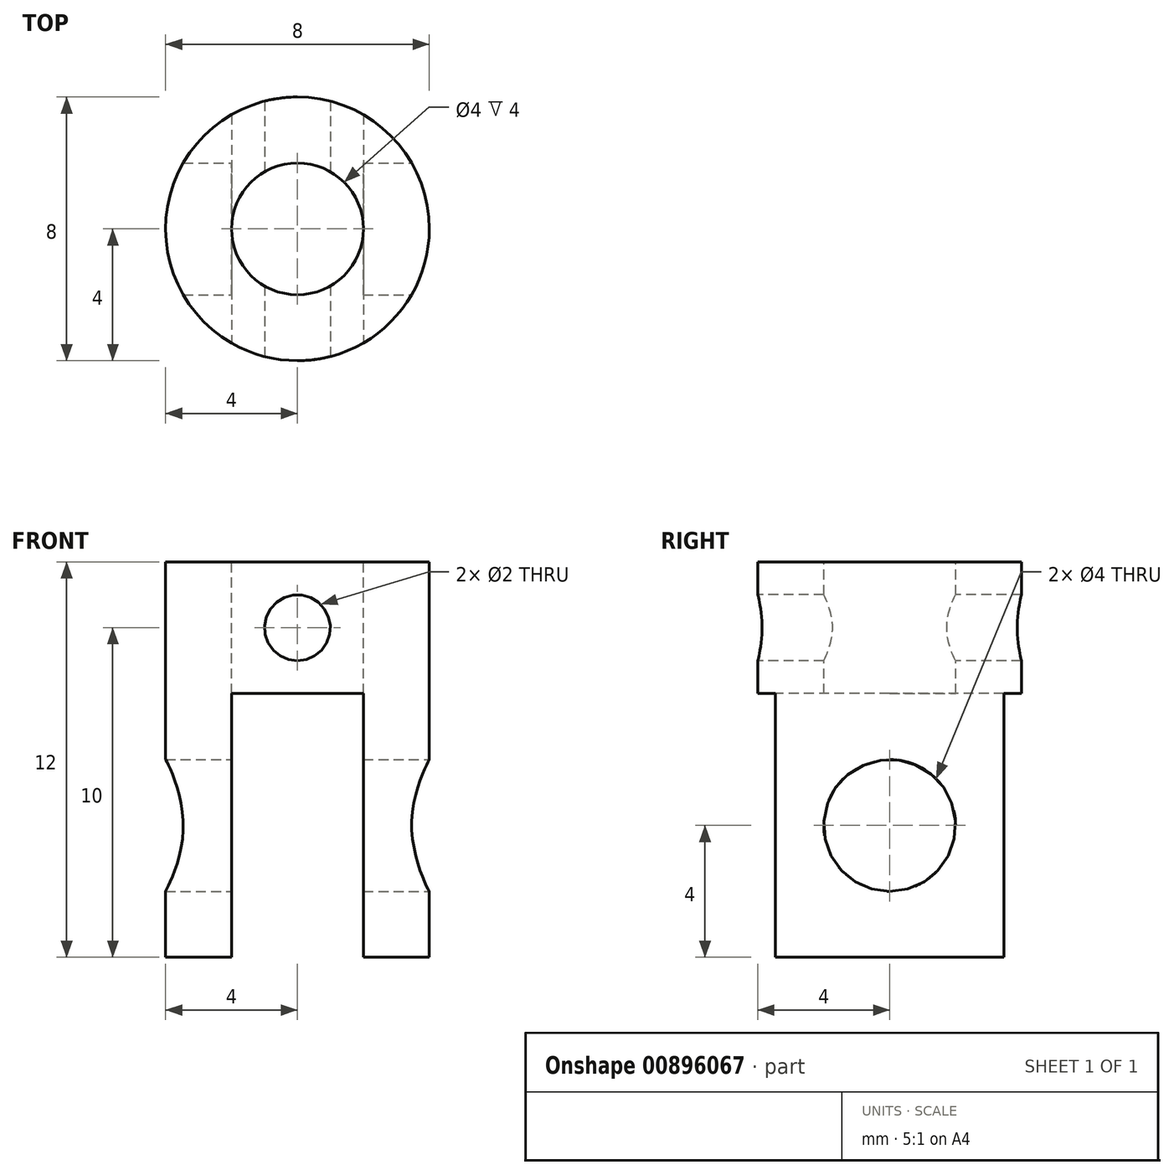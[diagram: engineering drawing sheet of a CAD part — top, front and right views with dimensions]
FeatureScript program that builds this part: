
annotation { "Feature Type Name" : "Feature", "Feature Type Description" : "" }
export const myFeature = defineFeature(function(context is Context, id is Id, definition is map)
    precondition{}
    {
        {
            var Q0;
            Q0=qCreatedBy(makeId("Top.planeOp"),FACE);
            var sketch = newSketch(context, id + "F0", { "sketchPlane" : qUnion([Q0])});
            skCircle(sketch, "E0", {"center": v(0, 0) * mm, "radius": 4 * mm});
            skSolve(sketch);
        }
        {
            var Q0;
            Q0 = qSketchRegion(id + "F0", true);
            extrude(context, id + "F1", {"entities" : qUnion([Q0]), "depth" : 12 * mm, "offsetDistance" : 25 * mm});
        }
        {
            var Q0;
            Q0=qCreatedBy(makeId("Front.planeOp"),FACE);
            var sketch = newSketch(context, id + "F2", { "sketchPlane" : qUnion([Q0])});
            skLineSegment(sketch, "E1.bottom", {"start": v(-2, 0) * mm, "end": v(2, 0) * mm});
            skLineSegment(sketch, "E1.top", {"start": v(-2, 8) * mm, "end": v(2, 8) * mm});
            skLineSegment(sketch, "E1.left", {"start": v(-2, 0) * mm, "end": v(-2, 8) * mm});
            skLineSegment(sketch, "E1.right", {"start": v(2, 0) * mm, "end": v(2, 8) * mm});
            skSolve(sketch);
        }
        {
            var Q0;
            Q0=makeQuery(id+"F2.imprint","IMPRINT",FACE,{"disambiguationData":[TD([[makeQuery(id+"F2.imprint","IMPRINT",EDGE,{"derivedFrom":sQuery(id+"F2.wireOp",EDGE,"E1.bottom")}),1.0]])]});
            extrude(context, id + "F3", {"entities" : qUnion([Q0]), "operationType" : NewBodyOperationType.REMOVE, "endBound" : BoundingType.SYMMETRIC, "oppositeDirection" : true, "depth" : 25 * mm, "offsetDistance" : 25 * mm});
        }
        {
            var Q0;
            Q0=qCreatedBy(makeId("Front.planeOp"),FACE);
            var sketch = newSketch(context, id + "F4", { "sketchPlane" : qUnion([Q0])});
            skCircle(sketch, "E2", {"center": v(0, 10) * mm, "radius": 1 * mm});
            skSolve(sketch);
        }
        {
            var Q0;
            Q0 = qSketchRegion(id + "F4", true);
            extrude(context, id + "F5", {"entities" : qUnion([Q0]), "operationType" : NewBodyOperationType.REMOVE, "endBound" : BoundingType.SYMMETRIC, "oppositeDirection" : true, "depth" : 25 * mm, "offsetDistance" : 25 * mm});
        }
        {
            var Q0;
            Q0=makeQuery(id+"F1.opExtrude","CAP_FACE",FACE,{"disambiguationData":[OSD([sQuery(id+"F0.wireOp",EDGE,"E0")])],"isStart":false});
            var sketch = newSketch(context, id + "F6", { "sketchPlane" : qUnion([Q0])});
            skCircle(sketch, "E3", {"center": v(0, 0) * mm, "radius": 2 * mm});
            skSolve(sketch);
        }
        {
            var Q0;
            Q0 = qSketchRegion(id + "F6", true);
            extrude(context, id + "F7", {"entities" : qUnion([Q0]), "operationType" : NewBodyOperationType.REMOVE, "endBound" : BoundingType.THROUGH_ALL, "oppositeDirection" : true, "depth" : 4 * mm, "offsetDistance" : 25 * mm});
        }
        {
            var Q0;
            Q0=qCreatedBy(makeId("Right.planeOp"),FACE);
            var sketch = newSketch(context, id + "F8", { "sketchPlane" : qUnion([Q0])});
            skCircle(sketch, "E4", {"center": v(0, 4) * mm, "radius": 2 * mm});
            skSolve(sketch);
        }
        {
            var Q0;
            Q0 = qSketchRegion(id + "F8", true);
            extrude(context, id + "F9", {"entities" : qUnion([Q0]), "operationType" : NewBodyOperationType.REMOVE, "endBound" : BoundingType.SYMMETRIC, "oppositeDirection" : true, "depth" : 25 * mm, "offsetDistance" : 25 * mm});
        }
    });
